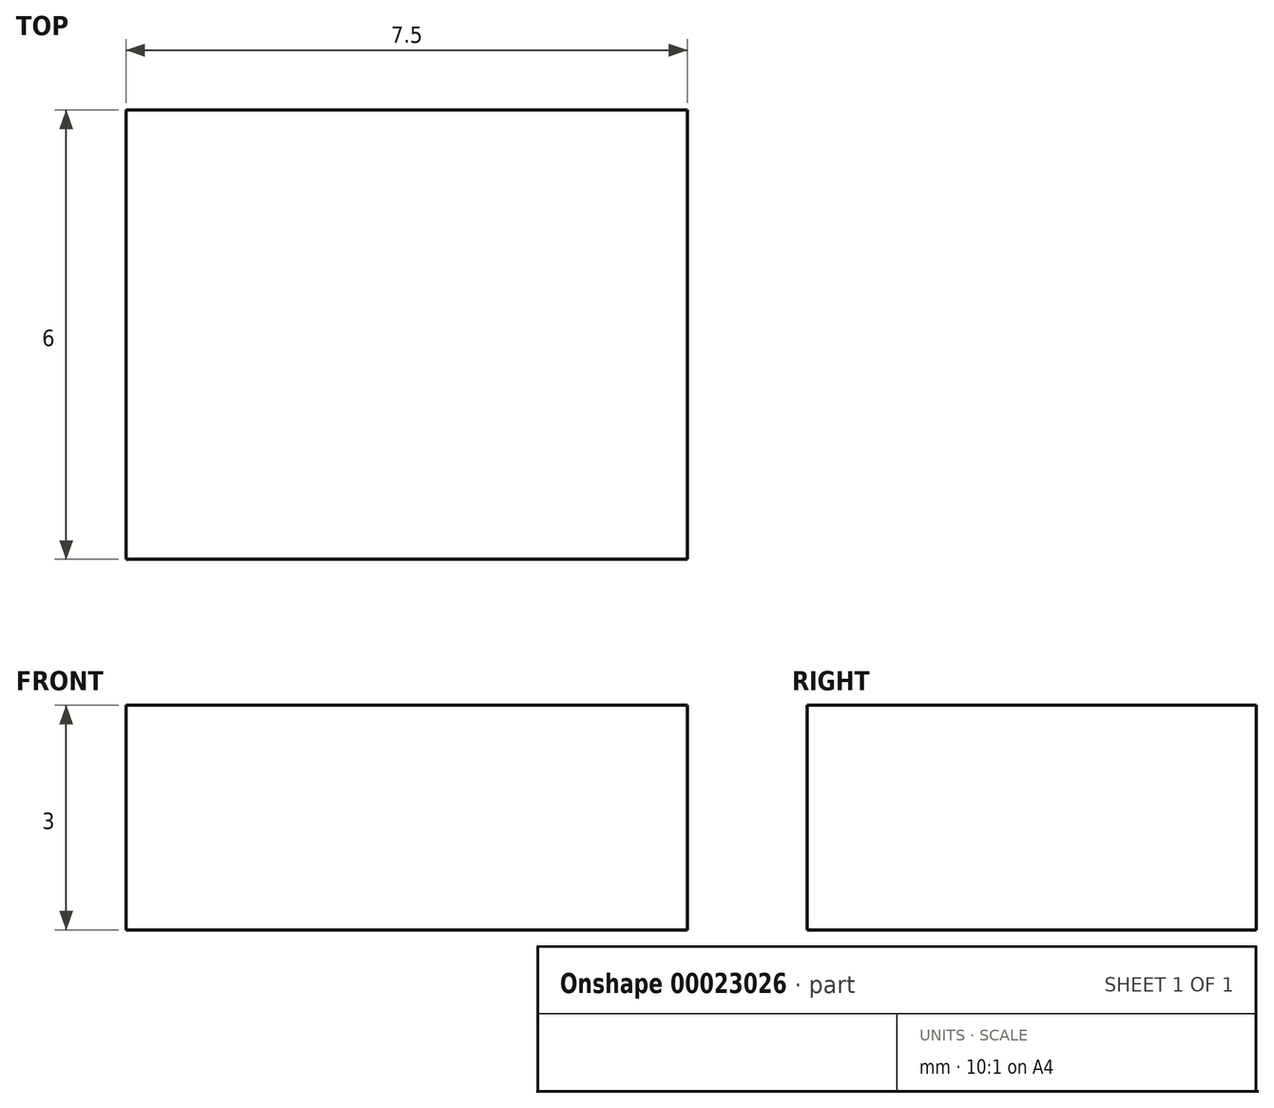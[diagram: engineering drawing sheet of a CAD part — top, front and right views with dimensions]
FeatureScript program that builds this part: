
annotation { "Feature Type Name" : "Feature", "Feature Type Description" : "" }
export const myFeature = defineFeature(function(context is Context, id is Id, definition is map)
    precondition{}
    {
        {
            var Q0;
            Q0=qCreatedBy(makeId("Top.planeOp"),FACE);
            var sketch = newSketch(context, id + "F0", { "sketchPlane" : qUnion([Q0])});
            skLineSegment(sketch, "E0.bottom", {"start": v(-3.75, 3) * mm, "end": v(3.75, 3) * mm});
            skLineSegment(sketch, "E0.top", {"start": v(-3.75, -3) * mm, "end": v(3.75, -3) * mm});
            skLineSegment(sketch, "E0.left", {"start": v(-3.75, 3) * mm, "end": v(-3.75, -3) * mm});
            skLineSegment(sketch, "E0.right", {"start": v(3.75, 3) * mm, "end": v(3.75, -3) * mm});
            skSolve(sketch);
        }
        {
            var Q0;
            Q0=makeQuery(id+"F0.imprint","IMPRINT",FACE,{"disambiguationData":[TD([[makeQuery(id+"F0.imprint","IMPRINT",EDGE,{"derivedFrom":sQuery(id+"F0.wireOp",EDGE,"E0.bottom")}),-1.0]])]});
            extrude(context, id + "F1", {"entities" : qUnion([Q0]), "depth" : 3 * mm});
        }
    });
